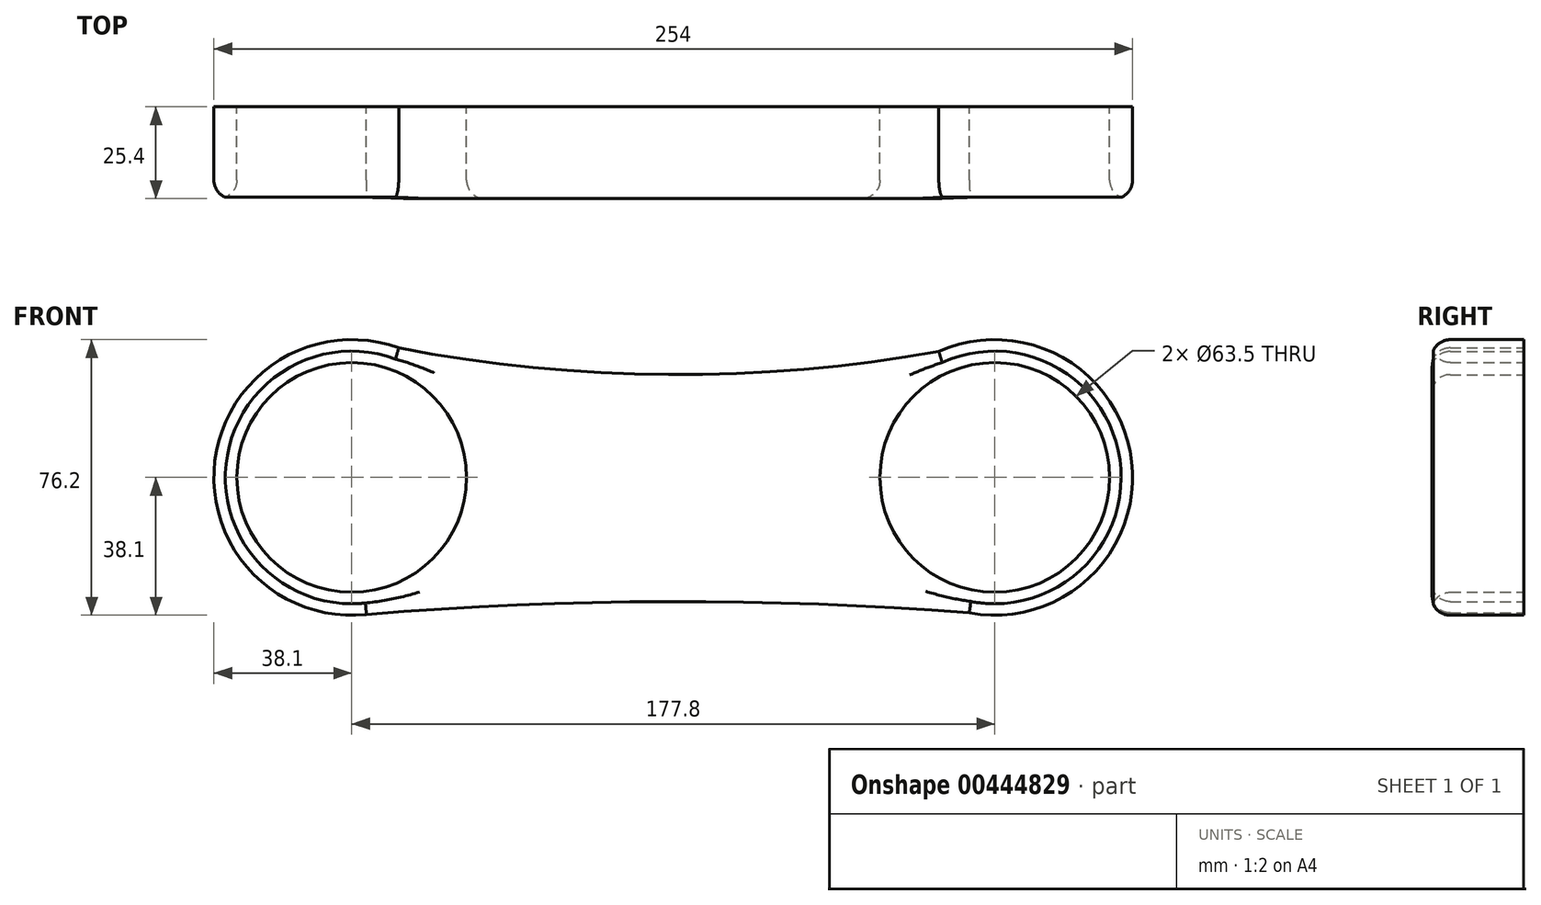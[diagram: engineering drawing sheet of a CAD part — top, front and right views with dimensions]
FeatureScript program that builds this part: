
annotation { "Feature Type Name" : "Feature", "Feature Type Description" : "" }
export const myFeature = defineFeature(function(context is Context, id is Id, definition is map)
    precondition{}
    {
        {
            var Q0;
            Q0=qCreatedBy(makeId("Front.planeOp"),FACE);
            var sketch = newSketch(context, id + "F0", { "sketchPlane" : qUnion([Q0])});
            skCircle(sketch, "E0", {"center": v(-88.9, 0) * mm, "radius": 38.1 * mm});
            skCircle(sketch, "E1", {"center": v(88.9, 0) * mm, "radius": 38.1 * mm});
            skArc(sketch, "E2", {"start": v(-86.63, 38.03) * mm, "mid": v(1.59, 28.43) * mm, "end": v(89.8, 38.09) * mm});
            skArc(sketch, "E3", {"start": v(89.8, -38.09) * mm, "mid": v(1.59, -34.32) * mm, "end": v(-86.63, -38.03) * mm});
            skCircle(sketch, "E4", {"center": v(-88.9, 0) * mm, "radius": 31.75 * mm});
            skCircle(sketch, "E5", {"center": v(88.9, 0) * mm, "radius": 31.75 * mm});
            skSolve(sketch);
        }
        {
            var Q0;
            Q0 = qSketchRegion(id + "F0", true);
            extrude(context, id + "F1", {"entities" : qUnion([Q0]), "depth" : 25.4 * mm});
        }
        {
            var Q0;
            Q0=makeQuery(id+"F1.opExtrude","CAP_FACE",FACE,{"disambiguationData":[OSD([sQuery(id+"F0.wireOp",EDGE,"E0"),sQuery(id+"F0.wireOp",EDGE,"E1"),sQuery(id+"F0.wireOp",EDGE,"E2"),sQuery(id+"F0.wireOp",EDGE,"E3"),sQuery(id+"F0.wireOp",EDGE,"E4"),sQuery(id+"F0.wireOp",EDGE,"E5")])],"isStart":false});
            fillet(context, id + "F2", {"entities" : qUnion([Q0]), "radius" : 5.08 * mm, "tangentPropagation" : true, "allowEdgeOverflow" : false});
        }
    });
